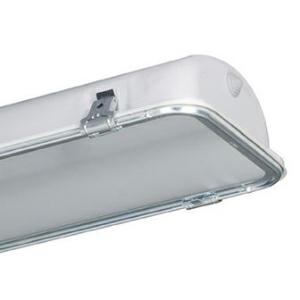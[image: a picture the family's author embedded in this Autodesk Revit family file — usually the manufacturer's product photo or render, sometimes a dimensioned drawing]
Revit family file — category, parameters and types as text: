
# Revit family: 3f_filippi_-_beta_i3f_76_vs_ampio_3f_filippi_-_55134_-_i3f_led_762x12w_ampio_vs_l655
name_source: partatom
category: Lighting Fixtures
units: mm (PartAtom-declared; Revit-internal decimal feet)

## family parameters
Cut with Voids When Loaded = No
Host = Face
Light Source = No
Part Type = Normal
Room Calculation Point = No
Round Connector Dimension = Use Diameter
Shared = No

## types (1)
- 3F Filippi - Beta i3F 76 VS Ampio (1 x LED, 3591 lm, 28 W, 4000 K)
    Apparent Load = 28 VA
    Approval mark = ENEC
    CIE Flux Codes = 62 90 98 100 100
    Color Rendering = 80
    Color Temperature = 4000 K
    Control Gear = Electronic ballast
    Default Elevation = 1800 mm
    Description = ILLUMINOTECHNICAL
Luminous efficiency 100% (DLOR 100%, ULOR 0%).
Initial luminous flux of the luminaire 3591 lm.
Wide symmetric distribution.
Installation Interdistance Transv.D = 1.31 x hu - Long.D = 1.31 x hu.
Tabular UGR (CIE 117 - 4H-8H; S=0.25H; 70/50/20): RUG 19.9 - 21.1.
Beam angle: 90° - 99°.
Luminous efficacy 128 lm/W.
Lifetime (L93/B10): 30000 h. (tq+25°C)
Lifetime (L90/B10): 50000 h. (tq+25°C)
Lifetime (L85/B10): 80000 h. (tq+25°C)
Lifetime (L80/B10): 100000 h. (tq+25°C)
Lifetime (L85/B10): 50000 h. (tq+35°C)
Sudden decreased luminous flux after 50000 hours: 0% (C0).
Photobiological safety in compliance with IEC/TR 62778: RG0 risk exempt, (IEC 62471).
In compliance with IEC/EN 62722-2-1 - IEC/EN 62717 standards.

SOURCE
2 linear LED modules 12W/840.
Energy efficiency class (UE 2019/2020 - UE 2019/2015): D.
CIE 13.3 Colour rendering index: CRI >80 (R9 <50%).
IES TM-30 Fidelity Index: Rf = 84 Rg = 95.
CCT nominal colour temperature 4000 K.
Colour initial tolerance (MacAdam): SDCM 3.

MECHANICAL
Single-piece housing in pressed steel, powder-coated in white epoxy-polyester.
Moulded anti-glare glass, non-combustible, tempered, mounted and locked to the single-piece galvanised steel perimetrical frame, sealing gasket, hinged opening by means of galvanised steel clips.
Wide flow recuperator, oversized, in specular aluminium with superficial titanium-magnesium treatment, non-iridescent.
Gear-tray unit in hot-galvanised steel, painted in white polyester, fixed to the housing by means of "Ribloc" rapid devices in galvanised steel, hinged opening.
Luminaire with limited surface temperature. - D - (EN 60598-2-24)
Dimensions: 655x235 mm, height 110 mm. Weight 4.385 kg.
IP65 protection degree.
Mechanical strength to impacts IK09 (10 joule).
Glow-wire test resistance 960°C.

ELECTRICAL
Halogen Free electronic wiring 230V-50/60Hz, power factor 0.90, THD <25%, constant output current, SELV, class I, 1 driver.
Power of the luminaire 28 W.
CE - IEC 60598-1 - EN 60598-1.
SAFE FLICKER: PstLM=<1 and SVM=<0.4 (IEC TR 61547-1 and IEC TR 63158), to ensure a more comfortable and safe light.
Luminaire compliant with EN 60598-2-22 for power supply from a centralised emergency system CPSS (Central Power Supply System), not incorporated in the luminaire - high risk areas excluded. The default power and flux are 100% in AC and 100% in DC.
Ambient temperature from -20°C to +35°C.
Temperature class T6 max 85°C.
Relative humidity UR: <85%.

INSTALLATION
Ceiling / Suspended / Wall.
All accessories dedicated to this product are available on the Catalog and on our website www.3F-Filippi.com.

APPLICATIONS
In industrial environments, stores and dry, dusty indoor environments, subject to occasional water splashes.

WARNING
Fixture not suitable for cold stores with an ambient temperature <0°C and/or relative humidity >85%.
Luminaire designed for disposal/recycling at end-of-life.
Replaceable (LED only) light source by a professional. Replaceable control gear by a professional.
    Height = 110 mm
    Lamp = 1 x LED
    Lamp Light Flux = 3591 lm
    Lamp Power = 28 W
    Lamp count = 1
    Length = 655 mm
    Lifetime = 50000 h
    Luminous efficacy = 128 lm/W
    Manufacturer = 3F Filippi
    ModVariant = No
    Model = 3F Filippi - 55134 - i3F LED 762x12W AMPIO VS L655
    Mounting Place = Ceiling
    Mounting Type = Pendant
    Number of Poles = 1
    OnlyDefault = Yes
    Power Factor = 1
    Product Name = 3F Filippi - Beta i3F 76 VS Ampio
    Product group = pendant luminaire
    ProductGroupID = 9
    Protection Class = Protection class I
    Protection Degree = IP 65
    RLX_Detail_Level = 1
    RLX_Emergency_Light_Flux = 0 lm
    RLX_Emergency_Type = 0
    RLX_Emergency_Type_DB = No
    RlxData = <blob elided: 62397 chars, md5=62148f9b>
    Socket = socket
    Standby Power = 0 W
    System Light Flux = 3591 lm
    System Power = 28 W
    Type Comments = Product without accessories
    Type Image = 3ffilippi_55134.jpg
    URL = http://relux.com
    VarID = ---
    Voltage = 0 V
    Weight = 0.00 kg
    Width = 235 mm

## geometry (parser evidence)
native form markers: Blend x4, Sweep x9
no freeform markers — native parametric forms only
